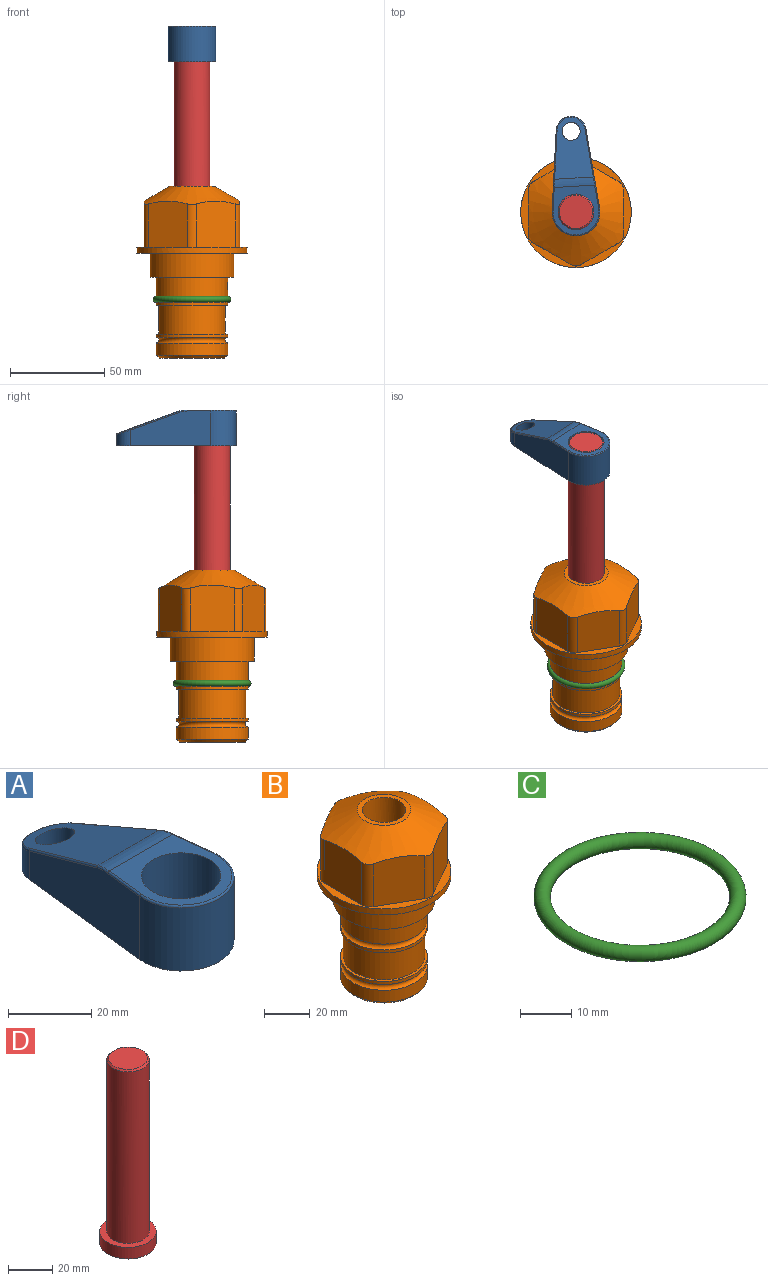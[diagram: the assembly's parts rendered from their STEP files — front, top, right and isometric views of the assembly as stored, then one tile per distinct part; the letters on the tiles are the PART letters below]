
ASSEMBLY  parts=4 mates=2
PART A: 44 faces, bbox 27.5x64.5x19.1 mm
  f0: plane 2.3x0.95mm, normal (0,0,-1), area 1mm2, adj f25,f30,f34
  f1: plane 63.5x25.4mm, normal (0,0,-1), area 561.7mm2, adj f2,f3,f4,f5,f6,f7,f19,f20
  f2: cylinder r=12.7mm len=25.4mm, axis (0,0,-1), area 792.2mm2, adj f1,f3,f5,f13
  f3: plane 42.33x18.54mm, normal (0.99,0.11,0), area 647mm2, adj f1,f2,f4,f11,f12,f14
  f4: cylinder r=7.94mm len=15.78mm, axis (0,0,-1), area 158.6mm2, adj f1,f3,f5,f16
  f5: plane 42.33x18.54mm, normal (-0.99,0.11,0), area 647mm2, adj f1,f2,f4,f15,f17,f18
  f6: cylinder r=9.53mm len=19.05mm, axis (0,0,-1), area 1140.1mm2, adj f1,f8
  f7: cylinder r=4.76mm len=10.98mm, axis (0,0,-1), area 276.1mm2, adj f1,f9
  f8: plane 25.83x24.38mm, normal (0,0,1), area 262.2mm2, adj f6,f10,f11,f13,f15
  f9: plane 32.49x20.55mm, normal (0,0.34,0.94), area 489.9mm2, adj f7,f10,f14,f16,f18
  f10: cylinder r=12.7mm len=21.49mm, axis (-1,0,0), area 93.2mm2, adj f8,f9,f12,f17
  f11: cylinder r=0.51mm len=12.34mm, axis (0.11,-0.99,0), area 9.9mm2, adj f3,f8,f12,f13
  f12: bspline ~7.62x1.64mm, area 3.5mm2, adj f3,f10,f11,f14
  f13: torus R=12.19mm, axis (0,0,1), area 33.6mm2, adj f2,f8,f11,f15
  f14: cylinder r=0.51mm len=26.01mm, axis (0.1,-0.93,0.34), area 21.6mm2, adj f3,f9,f12,f16
  f15: cylinder r=0.51mm len=12.34mm, axis (0.11,0.99,0), area 9.9mm2, adj f5,f8,f13,f17
  f16: bspline ~15.78x7.05mm, area 15.7mm2, adj f4,f9,f14,f18
  f17: bspline ~7.62x1.64mm, area 3.5mm2, adj f5,f10,f15,f18
  f18: cylinder r=0.51mm len=26.01mm, axis (0.1,0.93,-0.34), area 21.6mm2, adj f5,f9,f16,f17
  f19: plane 21.6x14.29mm, normal (-0.99,-0.11,0), area 242.6mm2, adj f1,f26,f28,f34,f36,f38
  f20: plane 21.6x14.29mm, normal (0.99,-0.11,0), area 242.6mm2, adj f1,f27,f29,f37,f39,f41
  f21: cylinder r=12.7mm len=14.29mm, axis (0,0,-1), area 173.2mm2, adj f1,f26,f27,f30,f31,f33
  f22: cylinder r=7.94mm len=7.63mm, axis (0,0,-1), area 53.8mm2, adj f1,f28,f29,f42
  f23: plane 2.3x0.95mm, normal (0,0,-1), area 1mm2, adj f25,f33,f37
  f24: plane 17.94x12.32mm, normal (0,-0.34,-0.94), area 191.2mm2, adj f25,f38,f41,f42
  f25: cylinder r=9.53mm len=12.93mm, axis (-1,0,0), area 37.5mm2, adj f0,f23,f24,f31,f36,f39
  f26: cylinder r=1.59mm len=14.29mm, axis (0,0,-1), area 49mm2, adj f1,f19,f21,f32
  f27: cylinder r=1.59mm len=14.29mm, axis (0,0,-1), area 49mm2, adj f1,f20,f21,f35
  f28: cylinder r=1.59mm len=7.28mm, axis (0,0,-1), area 22.1mm2, adj f1,f19,f22,f40
  f29: cylinder r=1.59mm len=7.28mm, axis (0,0,-1), area 22.1mm2, adj f1,f20,f22,f43
  f30: torus R=14.29mm, axis (0,0,1), area 5.8mm2, adj f0,f21,f31,f32
  f31: bspline ~11.06x2.73mm, area 20.8mm2, adj f21,f25,f30,f33
  f32: sphere r=1.59mm, area 5.4mm2, adj f26,f30,f34
  f33: torus R=14.29mm, axis (0,0,1), area 5.8mm2, adj f21,f23,f31,f35
  f34: cylinder r=1.59mm len=1.68mm, axis (-0.11,0.99,0), area 2.4mm2, adj f0,f19,f32,f36
  f35: sphere r=1.59mm, area 5.4mm2, adj f27,f33,f37
  f36: bspline ~5.82x2.33mm, area 7.7mm2, adj f19,f25,f34,f38
  f37: cylinder r=1.59mm len=1.68mm, axis (0.11,0.99,0), area 2.4mm2, adj f20,f23,f35,f39
  f38: cylinder r=1.59mm len=18.33mm, axis (0.1,-0.93,0.34), area 46.7mm2, adj f19,f24,f36,f40
  f39: bspline ~5.82x2.33mm, area 7.7mm2, adj f20,f25,f37,f41
  f40: sphere r=1.59mm, area 3.6mm2, adj f28,f38,f42
  f41: cylinder r=1.59mm len=18.33mm, axis (0.1,0.93,-0.34), area 46.7mm2, adj f20,f24,f39,f43
  f42: bspline ~8.31x1.84mm, area 15.3mm2, adj f22,f24,f40,f43
  f43: sphere r=1.59mm, area 3.6mm2, adj f29,f41,f42
PART B: 36 faces, bbox 58.7x58.7x91.2 mm
  f0: cylinder r=17.78mm len=35.56mm, axis (0,0,1), area 1670.8mm2, adj f23,f24,f31
  f1: cylinder r=19.05mm len=38.1mm, axis (0,0,1), area 1191.9mm2, adj f26,f27,f30
  f2: plane 58.66x58.66mm, normal (0,0,-1), area 1150.6mm2, adj f3,f28
  f3: cylinder r=29.33mm len=58.66mm, axis (0,0,-1), area 585.1mm2, adj f2,f4
  f4: plane 58.66x58.66mm, normal (0,0,1), area 475.9mm2, adj f3,f5,f6,f7,f8,f9,f10,f11
  f5: plane 24.5x20.32mm, normal (-0.5,0.87,0), area 562.8mm2, adj f4,f15,f16,f17
  f6: plane 24.5x20.32mm, normal (0.5,0.87,0), area 562.8mm2, adj f4,f14,f15,f17
  f7: plane 24.5x23.48mm, normal (1,0,0), area 562.8mm2, adj f4,f13,f14,f17
  f8: plane 24.5x20.32mm, normal (0.5,-0.87,0), area 562.8mm2, adj f4,f12,f13,f17
  f9: plane 24.5x20.32mm, normal (-0.5,-0.87,0), area 562.8mm2, adj f4,f11,f12,f17
  f10: plane 24.5x23.48mm, normal (-1,0,0), area 562.8mm2, adj f4,f11,f16,f17
  f11: cylinder r=5.08mm len=23.01mm, axis (0,0,-1), area 121.2mm2, adj f4,f9,f10,f17
  f12: cylinder r=5.08mm len=23.01mm, axis (0,0,-1), area 121.2mm2, adj f4,f8,f9,f17
  f13: cylinder r=5.08mm len=23.01mm, axis (0,0,-1), area 121.2mm2, adj f4,f7,f8,f17
  f14: cylinder r=5.08mm len=23.01mm, axis (0,0,-1), area 121.2mm2, adj f4,f6,f7,f17
  f15: cylinder r=5.08mm len=23.01mm, axis (0,0,-1), area 121.2mm2, adj f4,f5,f6,f17
  f16: cylinder r=5.08mm len=23.01mm, axis (0,0,-1), area 121.2mm2, adj f4,f5,f10,f17
  f17: cone r=11.73mm half-angle=60deg, axis (0,0,-1), area 2071.8mm2, adj f5,f6,f7,f8,f9,f10,f11,f12
  f18: plane 23.46x23.46mm, normal (0,0,1), area 147.4mm2, adj f17,f35
  f19: plane 34.93x34.93mm, normal (0,0,-1), area 958mm2, adj f29
  f20: cylinder r=19.05mm len=38.1mm, axis (0,0,1), area 760.1mm2, adj f21,f29
  f21: torus R=19.05mm, axis (0,0,1), area 565.3mm2, adj f20,f22
  f22: cylinder r=19.05mm len=38.1mm, axis (0,0,1), area 190mm2, adj f21,f23
  f23: plane 38.1x38.1mm, normal (0,0,1), area 146.9mm2, adj f0,f22
  f24: plane 38.1x38.1mm, normal (0,0,-1), area 146.9mm2, adj f0,f25
  f25: cylinder r=19.05mm len=38.1mm, axis (0,0,1), area 190mm2, adj f24,f26
  f26: torus R=19.05mm, axis (0,0,1), area 565.3mm2, adj f1,f25
  f27: plane 44.45x44.45mm, normal (0,0,-1), area 411.7mm2, adj f1,f28
  f28: cylinder r=22.23mm len=44.45mm, axis (0,0,1), area 1773.5mm2, adj f2,f27
  f29: cone r=19.05mm half-angle=45deg, axis (0,0,1), area 257.5mm2, adj f19,f20
  f30: cylinder r=3.17mm len=6.75mm, axis (-1,0,0), area 128mm2, adj f1,f33
  f31: cylinder r=3.17mm len=6.35mm, axis (-1,0,0), area 102.5mm2, adj f0,f33
  f32: plane 25.4x25.4mm, normal (0,0,1), area 506.7mm2, adj f33
  f33: cylinder r=12.7mm len=66.42mm, axis (0,0,-1), area 5236.2mm2, adj f30,f31,f32,f34
  f34: cone r=9.53mm half-angle=30deg, axis (0,0,-1), area 443.4mm2, adj f33,f35
  f35: cylinder r=9.53mm len=19.05mm, axis (0,0,-1), area 849mm2, adj f18,f34
PART C: 1 faces, bbox 44.7x44.7x3.2 mm
  f0: torus R=19.05mm, axis (0,0,1), area 1193.9mm2
PART D: 6 faces, bbox 25.4x25.4x101.6 mm
  f0: plane 17.46x17.46mm, normal (0,0,1), area 239.5mm2, adj f5
  f1: plane 25.4x25.4mm, normal (0,0,-1), area 506.7mm2, adj f2
  f2: cylinder r=12.7mm len=25.4mm, axis (0,0,1), area 506.7mm2, adj f1,f3
  f3: plane 25.4x25.4mm, normal (0,0,1), area 221.7mm2, adj f2,f4
  f4: cylinder r=9.53mm len=94.46mm, axis (0,0,1), area 5653mm2, adj f3,f5
  f5: cone r=8.73mm half-angle=45deg, axis (0,0,-1), area 64.4mm2, adj f0,f4
PLACE A rot(axis=(0,0,1),3.5deg) t=(0,0,101.53)mm
PLACE B at identity fixed
PLACE C at identity
PLACE D rot(axis=(0,0,1),93.5deg) t=(0,0,46.92)mm
MATE cylindrical D.f2 <-> B.f0  axis (0,0,1) through (0,0,72.56)mm
MATE fastened A.f2 <-> D.f2  axis (0,0,-1) through (0,0,120.58)mm
